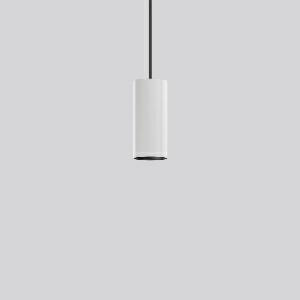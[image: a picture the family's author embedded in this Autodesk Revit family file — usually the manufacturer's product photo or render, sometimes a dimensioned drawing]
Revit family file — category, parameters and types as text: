
# Revit family: deecos_p_mini_911513_002_2_529c
name_source: partatom
category: Lighting Fixtures
units: mm (PartAtom-declared; Revit-internal decimal feet)

## family parameters
Cut with Voids When Loaded = No
Host = Face
Light Source = No
Part Type = Normal
Room Calculation Point = No
Round Connector Dimension = Use Diameter
Shared = No

## types (1)
- DEECOS P mini (1 x LED Modul 927, 2400 lm, 2700)
    Apparent Load = 20 VA
    Approval mark = CE
    CIE Flux Codes = 100 100 100 100 100
    Color Rendering = 92
    Color Temperature = 2700
    Default Elevation = 1800 mm
    Description = Series: DEECOS P mini
Cylindrical pendant luminaire. Housing: die-cast aluminium, powder-coated. Canopy made of powder-coated sheet steel with magnetic attachment. Optical assembly with reflector made of MIRO-Silver with 98% total light reflection for outstanding efficiency - can be changed without tools. Best colour rendering index Ra>90. Transparent pendant cable 5 m, can be shortened, with integrated steel cable. High quality converter without flickering and stroboscopic effect. The following accessories can be mounted without use of tools: interchangeable lenses, honeycomb louvre, clear and frosted diffusers, white interchangeable plastic ring. Decorative recessed suspension set available as accessory.Suitable for accessory Deecos P Tube cylinder extensions 0.5 m, 0.75 m or 1 m. 
Colour: traffic white, matt (RAL 9016)
Diameter: 87 mm
Height: 195 mm
Suspension length: 5000 mm
Lamp: LED
Socket: without socket
Colour temperature: 2700K
Colour rendering index (CRI): 92
System power: 20 W
Rated luminous flux: 2400 lm
Luminous efficiency: 120 lm/W
Control gear: Regulated power supply
Protection class: I
Type of protection: IP 20
    Height = 195 mm
    Lamp = 1 x LED Modul 927
    Lamp Light Flux = 2400 lm
    Lamp count = 1
    Length = 87 mm
    Lifetime = 50000 h
    Luminous efficacy = 120 lm/W
    Manufacturer = RZB
    ModVariant = No
    Model = 911513.002.2
    Mounting Place = Ceiling
    Mounting Type = Pendant
    Number of Poles = 1
    OnlyDefault = Yes
    Power Factor = 1
    Product Name = DEECOS P mini
    Product group = Pendant luminaires
    ProductGroupID = 902
    Protection Class = Protection class I
    Protection Degree = IP 20
    RLX_Detail_Level = 1
    RLX_Emergency_Light_Flux = 0 lm
    RLX_Emergency_Type = 0
    RLX_Emergency_Type_DB = No
    RlxData = <blob elided: 55145 chars, md5=beba5b14>
    Socket = socket
    Standby Power = 0 W
    System Light Flux = 2400 lm
    System Power = 20 W
    Type Comments = Product without accessories
    Type Image = 911476.002.jpg
    URL = http://relux.com
    VarID = ---
    Voltage = 230 V
    Voltage Range = 220-240 V
    Weight = 0.00 kg
    Width = 0 mm  [stored 0 ft]

note: [stored X ft] marks values corroborated as IEEE doubles in the binary element streams (Revit-internal decimal feet)

## geometry (parser evidence)
native form markers: Blend x4, Sweep x14
no freeform markers — native parametric forms only
